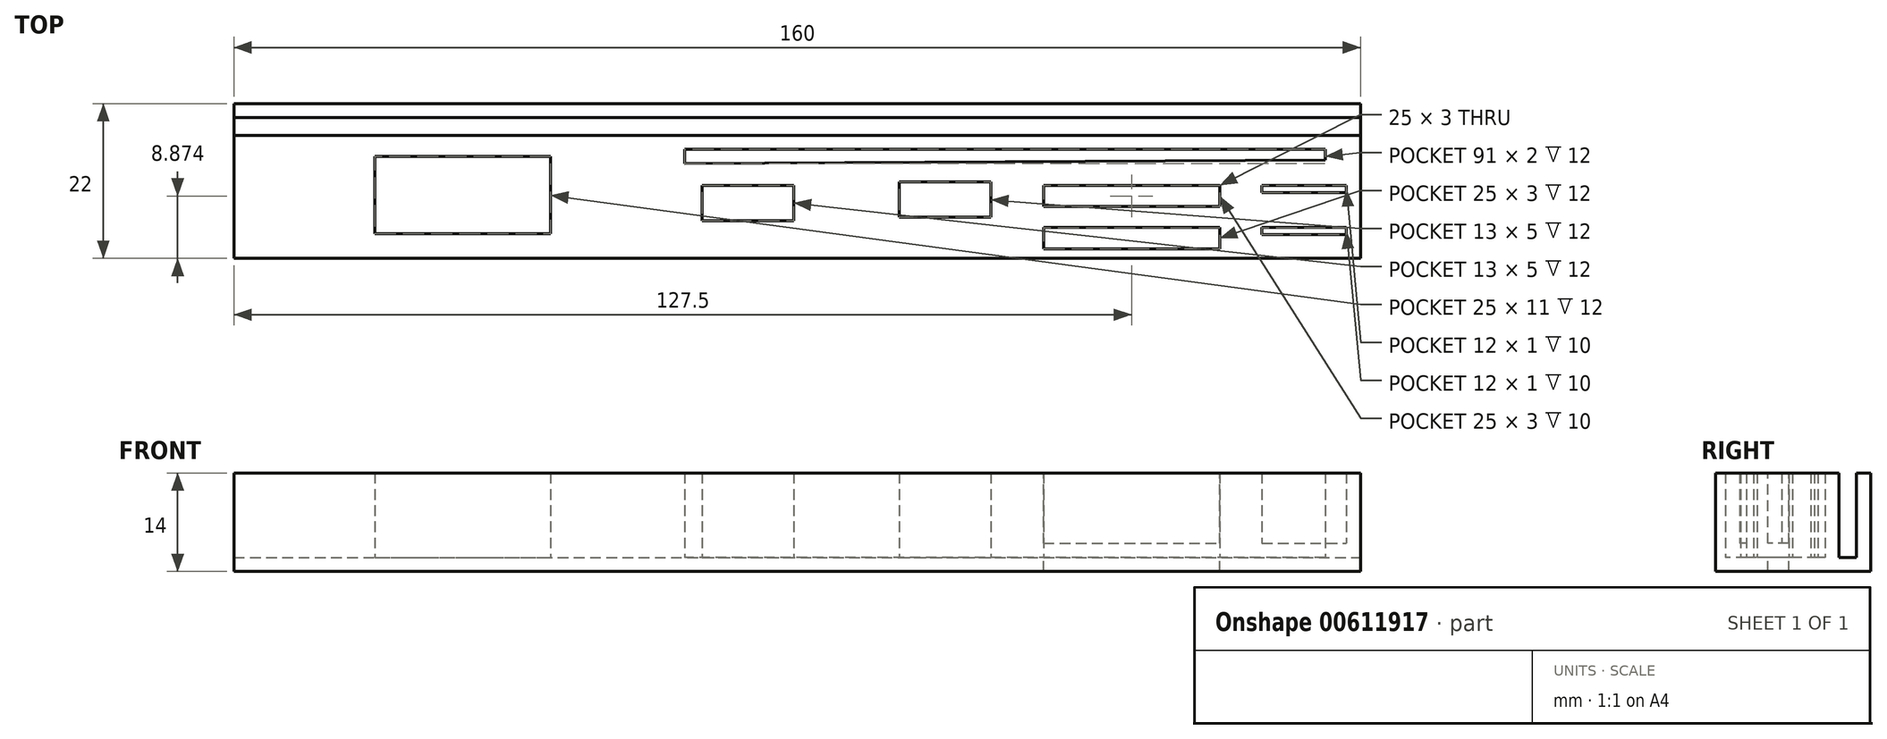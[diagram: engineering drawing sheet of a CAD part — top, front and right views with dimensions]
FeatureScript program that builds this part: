
annotation { "Feature Type Name" : "Feature", "Feature Type Description" : "" }
export const myFeature = defineFeature(function(context is Context, id is Id, definition is map)
    precondition{}
    {
        {
            var Q0;
            Q0=qCreatedBy(makeId("Top.planeOp"),FACE);
            var sketch = newSketch(context, id + "F0", { "sketchPlane" : qUnion([Q0])});
            skLineSegment(sketch, "E0.bottom", {"start": v(-115.2, 42.57) * mm, "end": v(44.8, 42.57) * mm});
            skLineSegment(sketch, "E0.top", {"start": v(-115.2, 20.57) * mm, "end": v(44.8, 20.57) * mm});
            skLineSegment(sketch, "E0.left", {"start": v(-115.2, 42.57) * mm, "end": v(-115.2, 20.57) * mm});
            skLineSegment(sketch, "E0.right", {"start": v(44.8, 42.57) * mm, "end": v(44.8, 20.57) * mm});
            skLineSegment(sketch, "E1.bottom", {"start": v(-115.2, 40.57) * mm, "end": v(44.8, 40.57) * mm});
            skLineSegment(sketch, "E1.top", {"start": v(-115.2, 38.07) * mm, "end": v(44.8, 38.07) * mm});
            skLineSegment(sketch, "E1.left", {"start": v(-115.2, 40.57) * mm, "end": v(-115.2, 38.07) * mm});
            skLineSegment(sketch, "E1.right", {"start": v(44.8, 40.57) * mm, "end": v(44.8, 38.07) * mm});
            skLineSegment(sketch, "E2.bottom", {"start": v(39.8, 36.07) * mm, "end": v(-51.2, 36.07) * mm});
            skLineSegment(sketch, "E2.top", {"start": v(39.8, 34.57) * mm, "end": v(-51.2, 34.07) * mm});
            skLineSegment(sketch, "E2.left", {"start": v(39.8, 36.07) * mm, "end": v(39.8, 34.57) * mm});
            skLineSegment(sketch, "E2.right", {"start": v(-51.2, 36.07) * mm, "end": v(-51.2, 34.07) * mm});
            skLineSegment(sketch, "E3.bottom", {"start": v(-95.2, 35.07) * mm, "end": v(-70.2, 35.07) * mm});
            skLineSegment(sketch, "E3.top", {"start": v(-95.2, 24.07) * mm, "end": v(-70.2, 24.07) * mm});
            skLineSegment(sketch, "E3.left", {"start": v(-95.2, 35.07) * mm, "end": v(-95.2, 24.07) * mm});
            skLineSegment(sketch, "E3.right", {"start": v(-70.2, 35.07) * mm, "end": v(-70.2, 24.07) * mm});
            skPoint(sketch, "E4", {"position": v(-82.7, 35.07) * mm});
            skLineSegment(sketch, "E5.bottom", {"start": v(-48.7, 30.94) * mm, "end": v(-35.7, 30.94) * mm});
            skLineSegment(sketch, "E5.top", {"start": v(-48.7, 25.94) * mm, "end": v(-35.7, 25.94) * mm});
            skLineSegment(sketch, "E5.left", {"start": v(-48.7, 30.94) * mm, "end": v(-48.7, 25.94) * mm});
            skLineSegment(sketch, "E5.right", {"start": v(-35.7, 30.94) * mm, "end": v(-35.7, 25.94) * mm});
            skPoint(sketch, "E6.firstSnap0", {"position": v(-35.7, 28.44) * mm});
            skLineSegment(sketch, "E7.bottom", {"start": v(-20.7, 31.44) * mm, "end": v(-7.7, 31.44) * mm});
            skLineSegment(sketch, "E7.top", {"start": v(-20.7, 26.44) * mm, "end": v(-7.7, 26.44) * mm});
            skLineSegment(sketch, "E7.left", {"start": v(-20.7, 31.44) * mm, "end": v(-20.7, 26.44) * mm});
            skLineSegment(sketch, "E7.right", {"start": v(-7.7, 31.44) * mm, "end": v(-7.7, 26.44) * mm});
            skLineSegment(sketch, "E8.bottom", {"start": v(-0.2, 24.94) * mm, "end": v(24.8, 24.94) * mm});
            skLineSegment(sketch, "E8.top", {"start": v(-0.2, 21.94) * mm, "end": v(24.8, 21.94) * mm});
            skLineSegment(sketch, "E8.left", {"start": v(-0.2, 24.94) * mm, "end": v(-0.2, 21.94) * mm});
            skLineSegment(sketch, "E8.right", {"start": v(24.8, 24.94) * mm, "end": v(24.8, 21.94) * mm});
            skLineSegment(sketch, "E9.bottom", {"start": v(30.8, 30.94) * mm, "end": v(42.8, 30.94) * mm});
            skLineSegment(sketch, "E9.top", {"start": v(30.8, 29.94) * mm, "end": v(42.8, 29.94) * mm});
            skLineSegment(sketch, "E9.left", {"start": v(30.8, 30.94) * mm, "end": v(30.8, 29.94) * mm});
            skLineSegment(sketch, "E9.right", {"start": v(42.8, 30.94) * mm, "end": v(42.8, 29.94) * mm});
            skLineSegment(sketch, "E10.bottom", {"start": v(30.8, 24.94) * mm, "end": v(42.8, 24.94) * mm});
            skLineSegment(sketch, "E10.top", {"start": v(30.8, 23.94) * mm, "end": v(42.8, 23.94) * mm});
            skLineSegment(sketch, "E10.left", {"start": v(30.8, 24.94) * mm, "end": v(30.8, 23.94) * mm});
            skLineSegment(sketch, "E10.right", {"start": v(42.8, 24.94) * mm, "end": v(42.8, 23.94) * mm});
            skLineSegment(sketch, "E11", {"start": v(-48.7, 30.94) * mm, "end": v(44.8, 30.94) * mm, "construction": true});
            skLineSegment(sketch, "E12.bottom", {"start": v(-0.2, 30.94) * mm, "end": v(24.8, 30.94) * mm});
            skLineSegment(sketch, "E12.top", {"start": v(-0.2, 27.94) * mm, "end": v(24.8, 27.94) * mm});
            skLineSegment(sketch, "E12.left", {"start": v(-0.2, 30.94) * mm, "end": v(-0.2, 27.94) * mm});
            skLineSegment(sketch, "E12.right", {"start": v(24.8, 30.94) * mm, "end": v(24.8, 27.94) * mm});
            skLineSegment(sketch, "E13", {"start": v(-0.2, 24.94) * mm, "end": v(44.8, 24.94) * mm, "construction": true});
            skSolve(sketch);
        }
        {
            var Q0;
            {var subQ0=sQuery(id+"F0.wireOp",EDGE,"E0.bottom");Q0=makeQuery(id+"F0.imprint","IMPRINT",FACE,{"disambiguationData":[TD([[makeQuery(id+"F0.imprint","IMPRINT",EDGE,{"derivedFrom":subQ0}),-1.0]])]});}
            var Q1;
            Q1=makeQuery(id+"F0.imprint","IMPRINT",FACE,{"disambiguationData":[TD([[makeQuery(id+"F0.imprint","IMPRINT",EDGE,{"derivedFrom":sQuery(id+"F0.wireOp",EDGE,"E1.bottom")}),-1.0]])]});
            var Q2;
            Q2=makeQuery(id+"F0.imprint","IMPRINT",FACE,{"disambiguationData":[TD([[makeQuery(id+"F0.imprint","IMPRINT",EDGE,{"derivedFrom":sQuery(id+"F0.wireOp",EDGE,"E3.bottom")}),-1.0]])]});
            var Q3;
            Q3=makeQuery(id+"F0.imprint","IMPRINT",FACE,{"disambiguationData":[TD([[makeQuery(id+"F0.imprint","IMPRINT",EDGE,{"derivedFrom":sQuery(id+"F0.wireOp",EDGE,"E2.bottom")}),1.0]])]});
            var Q4;
            Q4=makeQuery(id+"F0.imprint","IMPRINT",FACE,{"disambiguationData":[TD([[makeQuery(id+"F0.imprint","IMPRINT",EDGE,{"derivedFrom":sQuery(id+"F0.wireOp",EDGE,"E5.bottom")}),-1.0]])]});
            var Q5;
            Q5=makeQuery(id+"F0.imprint","IMPRINT",FACE,{"disambiguationData":[TD([[makeQuery(id+"F0.imprint","IMPRINT",EDGE,{"derivedFrom":sQuery(id+"F0.wireOp",EDGE,"WGVMys1t-UTvf-2Jmi-4lgg-94wHlsR6Uzpi.bottom")}),-1.0]])]});
            var Q6;
            Q6=makeQuery(id+"F0.imprint","IMPRINT",FACE,{"disambiguationData":[TD([[makeQuery(id+"F0.imprint","IMPRINT",EDGE,{"derivedFrom":sQuery(id+"F0.wireOp",EDGE,"E7.bottom")}),-1.0]])]});
            var Q7;
            Q7=makeQuery(id+"F0.imprint","IMPRINT",FACE,{"disambiguationData":[TD([[makeQuery(id+"F0.imprint","IMPRINT",EDGE,{"derivedFrom":sQuery(id+"F0.wireOp",EDGE,"bUfzkZVh-iGyp-XLFT-Os3q-JJTRM63qgp1C.bottom")}),-1.0]])]});
            var Q8;
            Q8=makeQuery(id+"F0.imprint","IMPRINT",FACE,{"disambiguationData":[TD([[makeQuery(id+"F0.imprint","IMPRINT",EDGE,{"derivedFrom":sQuery(id+"F0.wireOp",EDGE,"lM2hZorr-ZD2b-ot0y-uGpf-bJNIwXIdtA49.bottom")}),-1.0]])]});
            var Q9;
            Q9=makeQuery(id+"F0.imprint","IMPRINT",FACE,{"disambiguationData":[TD([[makeQuery(id+"F0.imprint","IMPRINT",EDGE,{"derivedFrom":sQuery(id+"F0.wireOp",EDGE,"E8.bottom")}),-1.0]])]});
            var Q10;
            Q10=makeQuery(id+"F0.imprint","IMPRINT",FACE,{"disambiguationData":[TD([[makeQuery(id+"F0.imprint","IMPRINT",EDGE,{"derivedFrom":sQuery(id+"F0.wireOp",EDGE,"a8LCvQb7-x1Wi-c7KR-Rm0v-G387zxVbhNoZ.bottom")}),-1.0]])]});
            var Q11;
            Q11=makeQuery(id+"F0.imprint","IMPRINT",FACE,{"disambiguationData":[TD([[makeQuery(id+"F0.imprint","IMPRINT",EDGE,{"derivedFrom":sQuery(id+"F0.wireOp",EDGE,"E10.bottom")}),-1.0]])]});
            var Q12;
            Q12=makeQuery(id+"F0.imprint","IMPRINT",FACE,{"disambiguationData":[TD([[makeQuery(id+"F0.imprint","IMPRINT",EDGE,{"derivedFrom":sQuery(id+"F0.wireOp",EDGE,"E9.bottom")}),-1.0]])]});
            var Q13;
            {var subQ0=sQuery(id+"F0.wireOp",EDGE,"E0.top");Q13=makeQuery(id+"F0.imprint","IMPRINT",FACE,{"disambiguationData":[TD([[makeQuery(id+"F0.imprint","IMPRINT",EDGE,{"derivedFrom":subQ0}),1.0]])]});}
            extrude(context, id + "F1", {"entities" : qUnion([Q0, Q1, Q2, Q3, Q4, Q5, Q6, Q7, Q8, Q9, Q10, Q11, Q12, Q13]), "depth" : -2 * mm, "offsetDistance" : 25 * mm});
        }
        {
            var Q0;
            {var subQ0=sQuery(id+"F0.wireOp",EDGE,"E0.top");Q0=makeQuery(id+"F0.imprint","IMPRINT",FACE,{"disambiguationData":[TD([[makeQuery(id+"F0.imprint","IMPRINT",EDGE,{"derivedFrom":subQ0}),1.0]])]});}
            var Q1;
            {var subQ0=sQuery(id+"F0.wireOp",EDGE,"E0.bottom");Q1=makeQuery(id+"F0.imprint","IMPRINT",FACE,{"disambiguationData":[TD([[makeQuery(id+"F0.imprint","IMPRINT",EDGE,{"derivedFrom":subQ0}),-1.0]])]});}
            extrude(context, id + "F2", {"entities" : qUnion([Q0, Q1]), "operationType" : NewBodyOperationType.ADD, "depth" : 12 * mm, "offsetDistance" : 25 * mm});
        }
        {
            var Q0;
            Q0=makeQuery(id+"F0.imprint","IMPRINT",FACE,{"disambiguationData":[TD([[makeQuery(id+"F0.imprint","IMPRINT",EDGE,{"derivedFrom":sQuery(id+"F0.wireOp",EDGE,"E9.bottom")}),-1.0]])]});
            var Q1;
            Q1=makeQuery(id+"F0.imprint","IMPRINT",FACE,{"disambiguationData":[TD([[makeQuery(id+"F0.imprint","IMPRINT",EDGE,{"derivedFrom":sQuery(id+"F0.wireOp",EDGE,"a8LCvQb7-x1Wi-c7KR-Rm0v-G387zxVbhNoZ.bottom")}),-1.0]])]});
            var Q2;
            Q2=makeQuery(id+"F0.imprint","IMPRINT",FACE,{"disambiguationData":[TD([[makeQuery(id+"F0.imprint","IMPRINT",EDGE,{"derivedFrom":sQuery(id+"F0.wireOp",EDGE,"E10.bottom")}),-1.0]])]});
            extrude(context, id + "F3", {"entities" : qUnion([Q0, Q1, Q2]), "operationType" : NewBodyOperationType.ADD, "depth" : 2 * mm, "offsetDistance" : 25 * mm});
        }
        {
            var Q0;
            Q0=makeQuery(id+"F0.imprint","IMPRINT",FACE,{"disambiguationData":[TD([[makeQuery(id+"F0.imprint","IMPRINT",EDGE,{"derivedFrom":sQuery(id+"F0.wireOp",EDGE,"E12.bottom")}),-1.0]])]});
            extrude(context, id + "F4", {"entities" : qUnion([Q0]), "operationType" : NewBodyOperationType.ADD, "depth" : 2 * mm, "offsetDistance" : 25 * mm});
        }
    });
